# Revit family: Ladder_Mini-Access_FIXFAST_RL22
name_source: partatom
category: Specialty Equipment
units: mm (PartAtom-declared; Revit-internal decimal feet)

## family parameters
Always vertical = No
Classification Number = 23.50.90.21
Cut with Voids When Loaded = No
Enable Cutting in Views = No
Maintain Annotation Orientation = No
Part Type = Normal
Room Calculation Point = No
Round Connector Dimension = Use Diameter
Shared = No
Work Plane-Based = Yes

## types (3) — shared parameters
Assembly Code = E1090900
Capacity = 330 lbs for High Frequency Usage
Default Elevation = 0' - 0"
Height Above Landing = 3' - 5 1/2"
Keynote = 05510
Manufacturer = FIXFAST USA
Manufacturer Fax = 317-769-5560
Manufacturer Website = http://www.fixfastusa.com
Overall Width = 1' - 11 1/2"
Product Data = http://www.arcat.com
Revision = R1_12-2013
Sales Information = http://www.fixfastusa.com
Send Message = http://www.arcat.com
Space Between Rungs = 1' - 0"
Standards Conformance = OSHA  ;  ANSI
URL = http://www.fixfastusa.com
Unit Width = 1' - 8 1/2"
zero-valued in all types: Expected Lifespan (Years), Maintenance Schedule (Months), Unit Weight, Warranty Duration (Years)

## per-type parameters (varying)
| type | Description | Maximum Size | Model |
| RL21.147 Full Ladder | FIXFAST KATT Mini Access Vertical Ladder - Parapet Crossover Kit RL21.147 | Heights up to 147 inches  (12' 3") | RL21.147 |
| RL21.100 Full Ladder | FIXFAST KATT Mini Access Vertical Ladder - Parapet Crossover Kit RL21.100 | Heights up to 100 inches  (8' 4") | RL21.100 |
| RL21.53 Full Ladder | FIXFAST KATT Mini Access Vertical Ladder - Parapet Crossover Kit RL21.53 | Heights up to 53 inches  (4' 5") | RL21.53 |

## geometry (parser evidence)
native form markers: Blend x4, Sweep x2
no freeform markers — native parametric forms only
